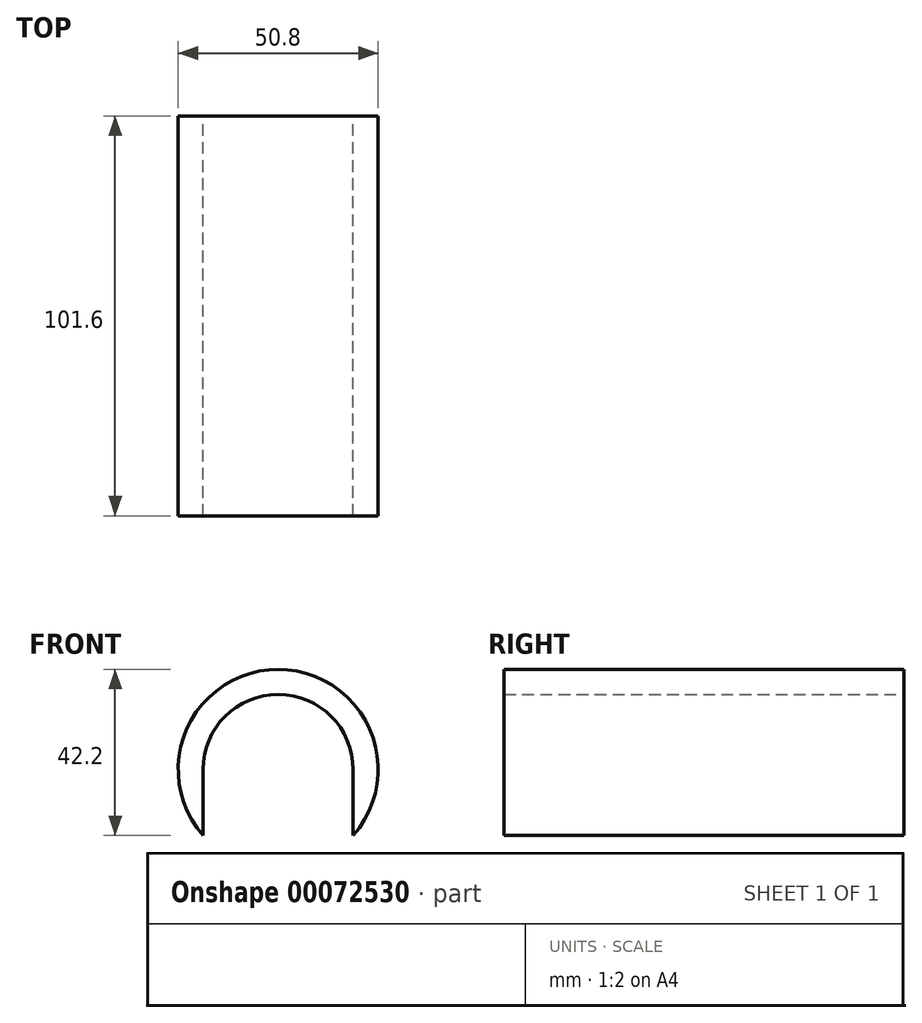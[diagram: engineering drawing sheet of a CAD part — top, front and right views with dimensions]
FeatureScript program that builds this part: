
annotation { "Feature Type Name" : "Feature", "Feature Type Description" : "" }
export const myFeature = defineFeature(function(context is Context, id is Id, definition is map)
    precondition{}
    {
        {
            var Q0;
            Q0=qCreatedBy(makeId("Front.planeOp"),FACE);
            var sketch = newSketch(context, id + "F0", { "sketchPlane" : qUnion([Q0])});
            skArc(sketch, "E0", {"start": v(19.05, -16.8) * mm, "mid": v(0, 25.4) * mm, "end": v(-19.05, -16.8) * mm});
            skLineSegment(sketch, "E1", {"start": v(0, 0) * mm, "end": v(19.05, 0) * mm, "construction": true});
            skArc(sketch, "E2", {"start": v(19.05, 0) * mm, "mid": v(0, 19.05) * mm, "end": v(-19.05, 0) * mm});
            skPoint(sketch, "E3.rect.middle", {"position": v(0, -19.05) * mm});
            skLineSegment(sketch, "E4", {"start": v(-19.05, -16.8) * mm, "end": v(-19.05, 0) * mm});
            skLineSegment(sketch, "E5", {"start": v(19.05, 0) * mm, "end": v(19.05, -16.8) * mm});
            skSolve(sketch);
        }
        {
            var Q0;
            Q0 = qSketchRegion(id + "F0", true);
            extrude(context, id + "F1", {"entities" : qUnion([Q0]), "depth" : 101.6 * mm});
        }
        {
            var Q0;
            Q0=makeQuery(id+"F1.opExtrude","SWEPT_FACE",FACE,{"disambiguationData":[OSD([sQuery(id+"F0.wireOp",EDGE,"E5")])]});
            cPlane(context, id + "F2", {"entities" : qUnion([Q0]), "cplaneType" : CPlaneType.OFFSET, "offset" : 6.35 * mm, "oppositeDirection" : true, "width" : 152.4 * mm, "height" : 152.4 * mm});
        }
    });
